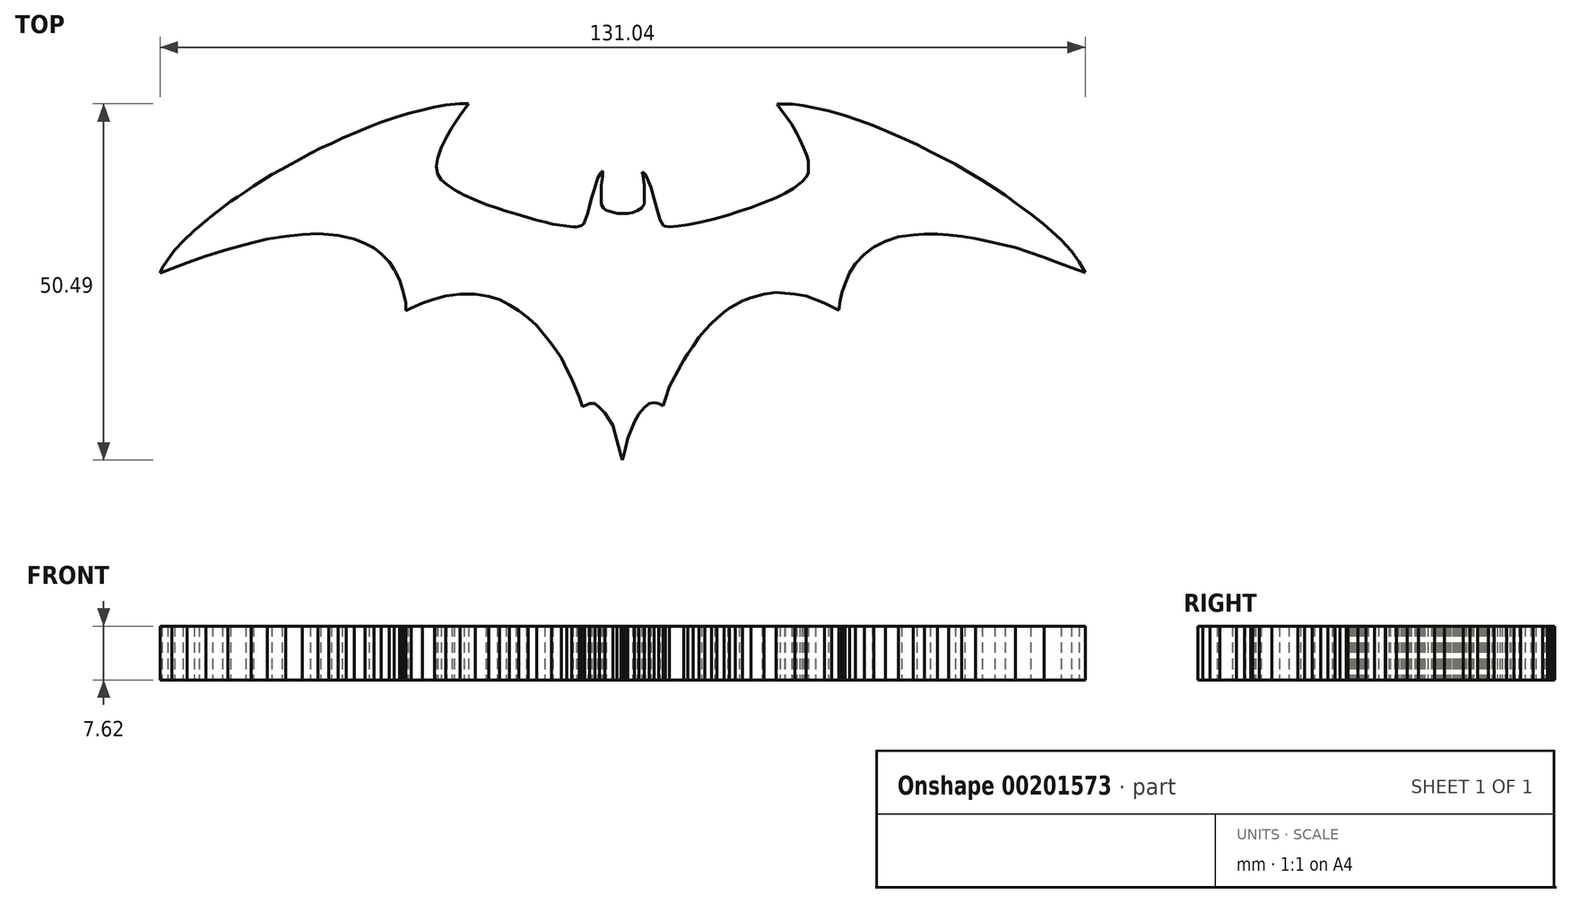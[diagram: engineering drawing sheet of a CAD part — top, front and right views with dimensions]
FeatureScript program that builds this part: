
annotation { "Feature Type Name" : "Feature", "Feature Type Description" : "" }
export const myFeature = defineFeature(function(context is Context, id is Id, definition is map)
    precondition{}
    {
        {
            var Q0;
            Q0=qCreatedBy(makeId("Top.planeOp"),FACE);
            var sketch = newSketch(context, id + "F0", { "sketchPlane" : qUnion([Q0])});
            skLineSegment(sketch, "E0", {"start": v(-30.4, 32.23) * mm, "end": v(-31.57, 30.6) * mm});
            skLineSegment(sketch, "E1", {"start": v(-31.57, 30.6) * mm, "end": v(-32.7, 28.9) * mm});
            skLineSegment(sketch, "E2", {"start": v(-32.7, 28.9) * mm, "end": v(-33.54, 27.45) * mm});
            skLineSegment(sketch, "E3", {"start": v(-33.54, 27.45) * mm, "end": v(-34.23, 26.04) * mm});
            skLineSegment(sketch, "E4", {"start": v(-34.23, 26.04) * mm, "end": v(-34.75, 24.53) * mm});
            skLineSegment(sketch, "E5", {"start": v(-34.75, 24.53) * mm, "end": v(-34.93, 23.39) * mm});
            skLineSegment(sketch, "E6", {"start": v(-34.93, 23.39) * mm, "end": v(-34.75, 22.26) * mm});
            skLineSegment(sketch, "E7", {"start": v(-34.75, 22.26) * mm, "end": v(-34.27, 21.5) * mm});
            skLineSegment(sketch, "E8", {"start": v(-34.27, 21.5) * mm, "end": v(-33.46, 20.8) * mm});
            skLineSegment(sketch, "E9", {"start": v(-33.46, 20.8) * mm, "end": v(-32.4, 20.05) * mm});
            skLineSegment(sketch, "E10", {"start": v(-32.4, 20.05) * mm, "end": v(-30.99, 19.32) * mm});
            skLineSegment(sketch, "E11", {"start": v(-30.99, 19.32) * mm, "end": v(-29.56, 18.68) * mm});
            skLineSegment(sketch, "E12", {"start": v(-29.56, 18.68) * mm, "end": v(-27.88, 18) * mm});
            skLineSegment(sketch, "E13", {"start": v(-27.88, 18) * mm, "end": v(-26.33, 17.45) * mm});
            skLineSegment(sketch, "E14", {"start": v(-26.33, 17.45) * mm, "end": v(-25.01, 17.02) * mm});
            skLineSegment(sketch, "E15", {"start": v(-25.01, 17.02) * mm, "end": v(-23.66, 16.6) * mm});
            skLineSegment(sketch, "E16", {"start": v(-23.66, 16.6) * mm, "end": v(-22.21, 16.2) * mm});
            skLineSegment(sketch, "E17", {"start": v(-22.21, 16.2) * mm, "end": v(-20.75, 15.73) * mm});
            skLineSegment(sketch, "E18", {"start": v(-20.75, 15.73) * mm, "end": v(-19.57, 15.52) * mm});
            skLineSegment(sketch, "E19", {"start": v(-19.57, 15.52) * mm, "end": v(-18.41, 15.18) * mm});
            skLineSegment(sketch, "E20", {"start": v(-18.41, 15.18) * mm, "end": v(-16.98, 14.98) * mm});
            skLineSegment(sketch, "E21", {"start": v(-16.98, 14.98) * mm, "end": v(-15.6, 14.8) * mm});
            skLineSegment(sketch, "E22", {"start": v(-15.6, 14.8) * mm, "end": v(-15.06, 14.8) * mm});
            skLineSegment(sketch, "E23", {"start": v(-15.06, 14.8) * mm, "end": v(-14.4, 14.97) * mm});
            skLineSegment(sketch, "E24", {"start": v(-14.4, 14.97) * mm, "end": v(-14.08, 15.22) * mm});
            skLineSegment(sketch, "E25", {"start": v(-14.08, 15.22) * mm, "end": v(-13.5, 16.75) * mm});
            skLineSegment(sketch, "E26", {"start": v(-13.5, 16.75) * mm, "end": v(-13.23, 17.86) * mm});
            skLineSegment(sketch, "E27", {"start": v(-13.23, 17.86) * mm, "end": v(-12.94, 19.07) * mm});
            skLineSegment(sketch, "E28", {"start": v(-12.94, 19.07) * mm, "end": v(-12.54, 20.18) * mm});
            skLineSegment(sketch, "E29", {"start": v(-12.54, 20.18) * mm, "end": v(-12.07, 21.7) * mm});
            skLineSegment(sketch, "E30", {"start": v(-12.07, 21.7) * mm, "end": v(-11.63, 22.4) * mm});
            skLineSegment(sketch, "E31", {"start": v(-11.63, 22.4) * mm, "end": v(-11.4, 22.7) * mm});
            skLineSegment(sketch, "E32", {"start": v(-11.4, 22.7) * mm, "end": v(-11.4, 21.93) * mm});
            skLineSegment(sketch, "E33", {"start": v(-11.4, 21.93) * mm, "end": v(-11.56, 20.69) * mm});
            skLineSegment(sketch, "E34", {"start": v(-11.56, 20.69) * mm, "end": v(-11.56, 18.7) * mm});
            skLineSegment(sketch, "E35", {"start": v(-11.56, 18.7) * mm, "end": v(-11.56, 17.94) * mm});
            skLineSegment(sketch, "E36", {"start": v(-11.56, 17.94) * mm, "end": v(-11.3, 17.44) * mm});
            skLineSegment(sketch, "E37", {"start": v(-11.3, 17.44) * mm, "end": v(-10.87, 17.18) * mm});
            skLineSegment(sketch, "E38", {"start": v(-10.87, 17.18) * mm, "end": v(-9.98, 16.9) * mm});
            skLineSegment(sketch, "E39", {"start": v(-9.98, 16.9) * mm, "end": v(-9.29, 16.68) * mm});
            skLineSegment(sketch, "E40", {"start": v(-9.29, 16.68) * mm, "end": v(-8.65, 16.68) * mm});
            skLineSegment(sketch, "E41", {"start": v(-8.65, 16.68) * mm, "end": v(-7.86, 16.68) * mm});
            skLineSegment(sketch, "E42", {"start": v(-7.86, 16.68) * mm, "end": v(-7.14, 16.84) * mm});
            skLineSegment(sketch, "E43", {"start": v(-7.14, 16.84) * mm, "end": v(-6.48, 17.1) * mm});
            skLineSegment(sketch, "E44", {"start": v(-6.48, 17.1) * mm, "end": v(-5.84, 17.46) * mm});
            skLineSegment(sketch, "E45", {"start": v(-5.84, 17.46) * mm, "end": v(-5.5, 18.01) * mm});
            skLineSegment(sketch, "E46", {"start": v(-5.5, 18.01) * mm, "end": v(-5.5, 18.92) * mm});
            skLineSegment(sketch, "E47", {"start": v(-5.5, 18.92) * mm, "end": v(-5.5, 19.81) * mm});
            skLineSegment(sketch, "E48", {"start": v(-5.5, 19.81) * mm, "end": v(-5.5, 20.69) * mm});
            skLineSegment(sketch, "E49", {"start": v(-5.5, 20.69) * mm, "end": v(-5.67, 22.08) * mm});
            skLineSegment(sketch, "E50", {"start": v(-5.67, 22.08) * mm, "end": v(-5.8, 22.63) * mm});
            skLineSegment(sketch, "E51", {"start": v(-5.8, 22.63) * mm, "end": v(-5.33, 22.3) * mm});
            skLineSegment(sketch, "E52", {"start": v(-5.33, 22.3) * mm, "end": v(-5.03, 21.6) * mm});
            skLineSegment(sketch, "E53", {"start": v(-5.03, 21.6) * mm, "end": v(-4.5, 20.4) * mm});
            skLineSegment(sketch, "E54", {"start": v(-4.5, 20.4) * mm, "end": v(-4.06, 18.73) * mm});
            skLineSegment(sketch, "E55", {"start": v(-4.06, 18.73) * mm, "end": v(-3.65, 17.16) * mm});
            skLineSegment(sketch, "E56", {"start": v(-3.65, 17.16) * mm, "end": v(-3.28, 15.8) * mm});
            skLineSegment(sketch, "E57", {"start": v(-3.28, 15.8) * mm, "end": v(-2.73, 14.9) * mm});
            skLineSegment(sketch, "E58", {"start": v(-2.73, 14.9) * mm, "end": v(-1.85, 14.78) * mm});
            skLineSegment(sketch, "E59", {"start": v(-1.85, 14.78) * mm, "end": v(-0.63, 14.93) * mm});
            skLineSegment(sketch, "E60", {"start": v(-0.63, 14.93) * mm, "end": v(0.75, 15.1) * mm});
            skLineSegment(sketch, "E61", {"start": v(0.75, 15.1) * mm, "end": v(2.63, 15.52) * mm});
            skLineSegment(sketch, "E62", {"start": v(2.63, 15.52) * mm, "end": v(4.47, 15.97) * mm});
            skLineSegment(sketch, "E63", {"start": v(4.47, 15.97) * mm, "end": v(6.31, 16.46) * mm});
            skLineSegment(sketch, "E64", {"start": v(6.31, 16.46) * mm, "end": v(7.95, 17.02) * mm});
            skLineSegment(sketch, "E65", {"start": v(7.95, 17.02) * mm, "end": v(9.65, 17.56) * mm});
            skLineSegment(sketch, "E66", {"start": v(9.65, 17.56) * mm, "end": v(11.24, 18.16) * mm});
            skLineSegment(sketch, "E67", {"start": v(11.24, 18.16) * mm, "end": v(13.16, 18.95) * mm});
            skLineSegment(sketch, "E68", {"start": v(13.16, 18.95) * mm, "end": v(14.45, 19.6) * mm});
            skLineSegment(sketch, "E69", {"start": v(14.45, 19.6) * mm, "end": v(15.69, 20.29) * mm});
            skLineSegment(sketch, "E70", {"start": v(15.69, 20.29) * mm, "end": v(16.88, 21.23) * mm});
            skLineSegment(sketch, "E71", {"start": v(16.88, 21.23) * mm, "end": v(17.5, 21.93) * mm});
            skLineSegment(sketch, "E72", {"start": v(17.5, 21.93) * mm, "end": v(17.77, 22.5) * mm});
            skLineSegment(sketch, "E73", {"start": v(17.77, 22.5) * mm, "end": v(17.77, 23) * mm});
            skLineSegment(sketch, "E74", {"start": v(17.77, 23) * mm, "end": v(17.77, 23.47) * mm});
            skLineSegment(sketch, "E75", {"start": v(17.77, 23.47) * mm, "end": v(17.77, 24.13) * mm});
            skLineSegment(sketch, "E76", {"start": v(17.77, 24.13) * mm, "end": v(17.57, 24.8) * mm});
            skLineSegment(sketch, "E77", {"start": v(17.57, 24.8) * mm, "end": v(17.15, 25.92) * mm});
            skLineSegment(sketch, "E78", {"start": v(17.15, 25.92) * mm, "end": v(16.55, 27.2) * mm});
            skLineSegment(sketch, "E79", {"start": v(16.55, 27.2) * mm, "end": v(16.09, 28.06) * mm});
            skLineSegment(sketch, "E80", {"start": v(16.09, 28.06) * mm, "end": v(15.38, 29.3) * mm});
            skLineSegment(sketch, "E81", {"start": v(15.38, 29.3) * mm, "end": v(14.4, 30.75) * mm});
            skLineSegment(sketch, "E82", {"start": v(14.4, 30.75) * mm, "end": v(13.76, 31.56) * mm});
            skLineSegment(sketch, "E83", {"start": v(13.76, 31.56) * mm, "end": v(13.34, 32.22) * mm});
            skLineSegment(sketch, "E84", {"start": v(13.34, 32.22) * mm, "end": v(15.52, 32.22) * mm});
            skLineSegment(sketch, "E85", {"start": v(15.52, 32.22) * mm, "end": v(16.91, 32.02) * mm});
            skLineSegment(sketch, "E86", {"start": v(16.91, 32.02) * mm, "end": v(18.77, 31.65) * mm});
            skLineSegment(sketch, "E87", {"start": v(18.77, 31.65) * mm, "end": v(20.59, 31.23) * mm});
            skLineSegment(sketch, "E88", {"start": v(20.59, 31.23) * mm, "end": v(22.8, 30.58) * mm});
            skLineSegment(sketch, "E89", {"start": v(22.8, 30.58) * mm, "end": v(24.85, 29.88) * mm});
            skLineSegment(sketch, "E90", {"start": v(24.85, 29.88) * mm, "end": v(26.81, 29.19) * mm});
            skLineSegment(sketch, "E91", {"start": v(26.81, 29.19) * mm, "end": v(29.05, 28.24) * mm});
            skLineSegment(sketch, "E92", {"start": v(29.05, 28.24) * mm, "end": v(30.97, 27.43) * mm});
            skLineSegment(sketch, "E93", {"start": v(30.97, 27.43) * mm, "end": v(33.1, 26.47) * mm});
            skLineSegment(sketch, "E94", {"start": v(33.1, 26.47) * mm, "end": v(35.01, 25.44) * mm});
            skLineSegment(sketch, "E95", {"start": v(35.01, 25.44) * mm, "end": v(36.8, 24.57) * mm});
            skLineSegment(sketch, "E96", {"start": v(36.8, 24.57) * mm, "end": v(38.6, 23.68) * mm});
            skLineSegment(sketch, "E97", {"start": v(38.6, 23.68) * mm, "end": v(39.93, 22.84) * mm});
            skLineSegment(sketch, "E98", {"start": v(39.93, 22.84) * mm, "end": v(42.38, 21.38) * mm});
            skLineSegment(sketch, "E99", {"start": v(42.38, 21.38) * mm, "end": v(44.2, 20.25) * mm});
            skLineSegment(sketch, "E100", {"start": v(44.2, 20.25) * mm, "end": v(45.63, 19.3) * mm});
            skLineSegment(sketch, "E101", {"start": v(45.63, 19.3) * mm, "end": v(47.5, 17.93) * mm});
            skLineSegment(sketch, "E102", {"start": v(47.5, 17.93) * mm, "end": v(49.23, 16.64) * mm});
            skLineSegment(sketch, "E103", {"start": v(49.23, 16.64) * mm, "end": v(51.06, 15.23) * mm});
            skLineSegment(sketch, "E104", {"start": v(51.06, 15.23) * mm, "end": v(52.26, 14.13) * mm});
            skLineSegment(sketch, "E105", {"start": v(52.26, 14.13) * mm, "end": v(53.55, 12.95) * mm});
            skLineSegment(sketch, "E106", {"start": v(53.55, 12.95) * mm, "end": v(55.05, 11.37) * mm});
            skLineSegment(sketch, "E107", {"start": v(55.05, 11.37) * mm, "end": v(56.1, 9.86) * mm});
            skLineSegment(sketch, "E108", {"start": v(56.1, 9.86) * mm, "end": v(56.97, 8.34) * mm});
            skLineSegment(sketch, "E109", {"start": v(56.97, 8.34) * mm, "end": v(55.04, 9.05) * mm});
            skLineSegment(sketch, "E110", {"start": v(55.04, 9.05) * mm, "end": v(52.82, 9.87) * mm});
            skLineSegment(sketch, "E111", {"start": v(52.82, 9.87) * mm, "end": v(51.15, 10.47) * mm});
            skLineSegment(sketch, "E112", {"start": v(51.15, 10.47) * mm, "end": v(48.93, 11.22) * mm});
            skLineSegment(sketch, "E113", {"start": v(48.93, 11.22) * mm, "end": v(47.1, 11.85) * mm});
            skLineSegment(sketch, "E114", {"start": v(47.1, 11.85) * mm, "end": v(45.24, 12.28) * mm});
            skLineSegment(sketch, "E115", {"start": v(45.24, 12.28) * mm, "end": v(42.95, 12.81) * mm});
            skLineSegment(sketch, "E116", {"start": v(42.95, 12.81) * mm, "end": v(41.42, 13.17) * mm});
            skLineSegment(sketch, "E117", {"start": v(41.42, 13.17) * mm, "end": v(39.45, 13.47) * mm});
            skLineSegment(sketch, "E118", {"start": v(39.45, 13.47) * mm, "end": v(37.64, 13.67) * mm});
            skLineSegment(sketch, "E119", {"start": v(37.64, 13.67) * mm, "end": v(36.02, 13.79) * mm});
            skLineSegment(sketch, "E120", {"start": v(36.02, 13.79) * mm, "end": v(34.22, 13.79) * mm});
            skLineSegment(sketch, "E121", {"start": v(34.22, 13.79) * mm, "end": v(32.62, 13.68) * mm});
            skLineSegment(sketch, "E122", {"start": v(32.62, 13.68) * mm, "end": v(30.51, 13.37) * mm});
            skLineSegment(sketch, "E123", {"start": v(30.51, 13.37) * mm, "end": v(28.66, 12.76) * mm});
            skLineSegment(sketch, "E124", {"start": v(28.66, 12.76) * mm, "end": v(27.06, 11.96) * mm});
            skLineSegment(sketch, "E125", {"start": v(27.06, 11.96) * mm, "end": v(25.68, 10.95) * mm});
            skLineSegment(sketch, "E126", {"start": v(25.68, 10.95) * mm, "end": v(24.4, 9.56) * mm});
            skLineSegment(sketch, "E127", {"start": v(24.4, 9.56) * mm, "end": v(23.63, 8.3) * mm});
            skLineSegment(sketch, "E128", {"start": v(23.63, 8.3) * mm, "end": v(22.94, 6.75) * mm});
            skLineSegment(sketch, "E129", {"start": v(22.94, 6.75) * mm, "end": v(22.51, 5.52) * mm});
            skLineSegment(sketch, "E130", {"start": v(22.51, 5.52) * mm, "end": v(22.29, 4.4) * mm});
            skLineSegment(sketch, "E131", {"start": v(22.29, 4.4) * mm, "end": v(22.1, 3) * mm});
            skLineSegment(sketch, "E132", {"start": v(22.1, 3) * mm, "end": v(21.07, 3.52) * mm});
            skLineSegment(sketch, "E133", {"start": v(21.07, 3.52) * mm, "end": v(20.03, 4.01) * mm});
            skLineSegment(sketch, "E134", {"start": v(20.03, 4.01) * mm, "end": v(18.8, 4.48) * mm});
            skLineSegment(sketch, "E135", {"start": v(18.8, 4.48) * mm, "end": v(17.43, 5) * mm});
            skLineSegment(sketch, "E136", {"start": v(17.43, 5) * mm, "end": v(15.87, 5.26) * mm});
            skLineSegment(sketch, "E137", {"start": v(15.87, 5.26) * mm, "end": v(14.49, 5.39) * mm});
            skLineSegment(sketch, "E138", {"start": v(14.49, 5.39) * mm, "end": v(13.17, 5.5) * mm});
            skLineSegment(sketch, "E139", {"start": v(13.17, 5.5) * mm, "end": v(11.44, 5.26) * mm});
            skLineSegment(sketch, "E140", {"start": v(11.44, 5.26) * mm, "end": v(9.66, 4.8) * mm});
            skLineSegment(sketch, "E141", {"start": v(9.66, 4.8) * mm, "end": v(8.41, 4.33) * mm});
            skLineSegment(sketch, "E142", {"start": v(8.41, 4.33) * mm, "end": v(7.44, 3.77) * mm});
            skLineSegment(sketch, "E143", {"start": v(7.44, 3.77) * mm, "end": v(6.59, 3.3) * mm});
            skLineSegment(sketch, "E144", {"start": v(6.59, 3.3) * mm, "end": v(5.8, 2.74) * mm});
            skLineSegment(sketch, "E145", {"start": v(5.8, 2.74) * mm, "end": v(4.8, 1.85) * mm});
            skLineSegment(sketch, "E146", {"start": v(4.8, 1.85) * mm, "end": v(4.07, 1.16) * mm});
            skLineSegment(sketch, "E147", {"start": v(4.07, 1.16) * mm, "end": v(3.12, 0.15) * mm});
            skLineSegment(sketch, "E148", {"start": v(3.12, 0.15) * mm, "end": v(2.26, -0.85) * mm});
            skLineSegment(sketch, "E149", {"start": v(2.26, -0.85) * mm, "end": v(1.4, -2.07) * mm});
            skLineSegment(sketch, "E150", {"start": v(1.4, -2.07) * mm, "end": v(0.67, -3.16) * mm});
            skLineSegment(sketch, "E151", {"start": v(0.67, -3.16) * mm, "end": v(0.13, -4.1) * mm});
            skLineSegment(sketch, "E152", {"start": v(0.13, -4.1) * mm, "end": v(-0.53, -5.3) * mm});
            skLineSegment(sketch, "E153", {"start": v(-0.53, -5.3) * mm, "end": v(-1.22, -6.55) * mm});
            skLineSegment(sketch, "E154", {"start": v(-1.22, -6.55) * mm, "end": v(-1.91, -7.81) * mm});
            skLineSegment(sketch, "E155", {"start": v(-1.91, -7.81) * mm, "end": v(-2.48, -9.6) * mm});
            skLineSegment(sketch, "E156", {"start": v(-2.48, -9.6) * mm, "end": v(-2.84, -10.55) * mm});
            skLineSegment(sketch, "E157", {"start": v(-2.84, -10.55) * mm, "end": v(-3.42, -10.23) * mm});
            skLineSegment(sketch, "E158", {"start": v(-3.42, -10.23) * mm, "end": v(-4.09, -10.09) * mm});
            skLineSegment(sketch, "E159", {"start": v(-4.09, -10.09) * mm, "end": v(-4.79, -10.23) * mm});
            skLineSegment(sketch, "E160", {"start": v(-4.79, -10.23) * mm, "end": v(-5.47, -10.79) * mm});
            skLineSegment(sketch, "E161", {"start": v(-5.47, -10.79) * mm, "end": v(-6.27, -11.7) * mm});
            skLineSegment(sketch, "E162", {"start": v(-6.27, -11.7) * mm, "end": v(-6.87, -12.8) * mm});
            skLineSegment(sketch, "E163", {"start": v(-6.87, -12.8) * mm, "end": v(-7.38, -14.08) * mm});
            skLineSegment(sketch, "E164", {"start": v(-7.38, -14.08) * mm, "end": v(-7.82, -15.18) * mm});
            skLineSegment(sketch, "E165", {"start": v(-7.82, -15.18) * mm, "end": v(-8.17, -16.57) * mm});
            skLineSegment(sketch, "E166", {"start": v(-8.17, -16.57) * mm, "end": v(-8.4, -17.6) * mm});
            skLineSegment(sketch, "E167", {"start": v(-8.8, -17.6) * mm, "end": v(-9.33, -15.52) * mm});
            skLineSegment(sketch, "E168", {"start": v(-9.33, -15.52) * mm, "end": v(-9.95, -13.36) * mm});
            skLineSegment(sketch, "E169", {"start": v(-9.95, -13.36) * mm, "end": v(-11.05, -11.58) * mm});
            skLineSegment(sketch, "E170", {"start": v(-11.05, -11.58) * mm, "end": v(-11.81, -10.79) * mm});
            skLineSegment(sketch, "E171", {"start": v(-11.81, -10.79) * mm, "end": v(-12.46, -10.23) * mm});
            skLineSegment(sketch, "E172", {"start": v(-12.46, -10.23) * mm, "end": v(-13.26, -10.23) * mm});
            skLineSegment(sketch, "E173", {"start": v(-13.26, -10.23) * mm, "end": v(-13.9, -10.52) * mm});
            skLineSegment(sketch, "E174", {"start": v(-13.9, -10.52) * mm, "end": v(-14.21, -10.66) * mm});
            skLineSegment(sketch, "E175", {"start": v(-14.21, -10.66) * mm, "end": v(-14.66, -9.32) * mm});
            skLineSegment(sketch, "E176", {"start": v(-14.66, -9.32) * mm, "end": v(-15.74, -6.73) * mm});
            skLineSegment(sketch, "E177", {"start": v(-15.74, -6.73) * mm, "end": v(-16.5, -5.4) * mm});
            skLineSegment(sketch, "E178", {"start": v(-16.5, -5.4) * mm, "end": v(-17.25, -3.76) * mm});
            skLineSegment(sketch, "E179", {"start": v(-17.25, -3.76) * mm, "end": v(-18.64, -1.74) * mm});
            skLineSegment(sketch, "E180", {"start": v(-18.64, -1.74) * mm, "end": v(-19.88, -0.22) * mm});
            skLineSegment(sketch, "E181", {"start": v(-19.88, -0.22) * mm, "end": v(-20.71, 0.8) * mm});
            skLineSegment(sketch, "E182", {"start": v(-20.71, 0.8) * mm, "end": v(-21.92, 1.88) * mm});
            skLineSegment(sketch, "E183", {"start": v(-21.92, 1.88) * mm, "end": v(-23.24, 2.91) * mm});
            skLineSegment(sketch, "E184", {"start": v(-23.24, 2.91) * mm, "end": v(-24.6, 3.77) * mm});
            skLineSegment(sketch, "E185", {"start": v(-24.6, 3.77) * mm, "end": v(-26.02, 4.53) * mm});
            skLineSegment(sketch, "E186", {"start": v(-26.02, 4.53) * mm, "end": v(-27.54, 4.94) * mm});
            skLineSegment(sketch, "E187", {"start": v(-27.54, 4.94) * mm, "end": v(-29.42, 5.3) * mm});
            skLineSegment(sketch, "E188", {"start": v(-29.42, 5.3) * mm, "end": v(-31.6, 5.3) * mm});
            skLineSegment(sketch, "E189", {"start": v(-31.6, 5.3) * mm, "end": v(-33.61, 5.04) * mm});
            skLineSegment(sketch, "E190", {"start": v(-33.61, 5.04) * mm, "end": v(-35.2, 4.6) * mm});
            skLineSegment(sketch, "E191", {"start": v(-35.2, 4.6) * mm, "end": v(-36.93, 3.98) * mm});
            skLineSegment(sketch, "E192", {"start": v(-36.93, 3.98) * mm, "end": v(-38.5, 3.28) * mm});
            skLineSegment(sketch, "E193", {"start": v(-38.5, 3.28) * mm, "end": v(-39.27, 2.91) * mm});
            skLineSegment(sketch, "E194", {"start": v(-39.27, 2.91) * mm, "end": v(-39.27, 4.04) * mm});
            skLineSegment(sketch, "E195", {"start": v(-39.27, 4.04) * mm, "end": v(-39.7, 5.87) * mm});
            skLineSegment(sketch, "E196", {"start": v(-39.7, 5.87) * mm, "end": v(-40.16, 7.33) * mm});
            skLineSegment(sketch, "E197", {"start": v(-40.16, 7.33) * mm, "end": v(-40.94, 8.77) * mm});
            skLineSegment(sketch, "E198", {"start": v(-40.94, 8.77) * mm, "end": v(-41.62, 9.85) * mm});
            skLineSegment(sketch, "E199", {"start": v(-41.62, 9.85) * mm, "end": v(-42.77, 10.98) * mm});
            skLineSegment(sketch, "E200", {"start": v(-42.77, 10.98) * mm, "end": v(-43.78, 11.83) * mm});
            skLineSegment(sketch, "E201", {"start": v(-43.78, 11.83) * mm, "end": v(-45.05, 12.48) * mm});
            skLineSegment(sketch, "E202", {"start": v(-45.05, 12.48) * mm, "end": v(-46.55, 13.07) * mm});
            skLineSegment(sketch, "E203", {"start": v(-46.55, 13.07) * mm, "end": v(-47.7, 13.35) * mm});
            skLineSegment(sketch, "E204", {"start": v(-47.7, 13.35) * mm, "end": v(-48.85, 13.57) * mm});
            skLineSegment(sketch, "E205", {"start": v(-48.85, 13.57) * mm, "end": v(-50.17, 13.73) * mm});
            skLineSegment(sketch, "E206", {"start": v(-50.17, 13.73) * mm, "end": v(-51.7, 13.87) * mm});
            skLineSegment(sketch, "E207", {"start": v(-51.7, 13.87) * mm, "end": v(-53.9, 13.72) * mm});
            skLineSegment(sketch, "E208", {"start": v(-53.9, 13.72) * mm, "end": v(-56.29, 13.5) * mm});
            skLineSegment(sketch, "E209", {"start": v(-56.29, 13.5) * mm, "end": v(-58.9, 13.07) * mm});
            skLineSegment(sketch, "E210", {"start": v(-58.9, 13.07) * mm, "end": v(-61.15, 12.54) * mm});
            skLineSegment(sketch, "E211", {"start": v(-61.15, 12.54) * mm, "end": v(-64.47, 11.63) * mm});
            skLineSegment(sketch, "E212", {"start": v(-64.47, 11.63) * mm, "end": v(-67.59, 10.67) * mm});
            skLineSegment(sketch, "E213", {"start": v(-67.59, 10.67) * mm, "end": v(-70.22, 9.74) * mm});
            skLineSegment(sketch, "E214", {"start": v(-70.22, 9.74) * mm, "end": v(-72.38, 8.87) * mm});
            skLineSegment(sketch, "E215", {"start": v(-72.38, 8.87) * mm, "end": v(-74.07, 8.28) * mm});
            skLineSegment(sketch, "E216", {"start": v(-74.07, 8.28) * mm, "end": v(-73.8, 8.96) * mm});
            skLineSegment(sketch, "E217", {"start": v(-73.8, 8.96) * mm, "end": v(-73, 10.16) * mm});
            skLineSegment(sketch, "E218", {"start": v(-73, 10.16) * mm, "end": v(-72.02, 11.52) * mm});
            skLineSegment(sketch, "E219", {"start": v(-72.02, 11.52) * mm, "end": v(-70.8, 12.75) * mm});
            skLineSegment(sketch, "E220", {"start": v(-70.8, 12.75) * mm, "end": v(-69.2, 14.3) * mm});
            skLineSegment(sketch, "E221", {"start": v(-69.2, 14.3) * mm, "end": v(-68.54, 14.86) * mm});
            skLineSegment(sketch, "E222", {"start": v(-68.54, 14.86) * mm, "end": v(-67.75, 15.54) * mm});
            skLineSegment(sketch, "E223", {"start": v(-67.75, 15.54) * mm, "end": v(-66.66, 16.46) * mm});
            skLineSegment(sketch, "E224", {"start": v(-66.66, 16.46) * mm, "end": v(-65.23, 17.5) * mm});
            skLineSegment(sketch, "E225", {"start": v(-65.23, 17.5) * mm, "end": v(-64.1, 18.42) * mm});
            skLineSegment(sketch, "E226", {"start": v(-64.1, 18.42) * mm, "end": v(-63.07, 19.07) * mm});
            skLineSegment(sketch, "E227", {"start": v(-63.07, 19.07) * mm, "end": v(-61.96, 19.79) * mm});
            skLineSegment(sketch, "E228", {"start": v(-61.96, 19.79) * mm, "end": v(-60.83, 20.58) * mm});
            skLineSegment(sketch, "E229", {"start": v(-60.83, 20.58) * mm, "end": v(-59.64, 21.34) * mm});
            skLineSegment(sketch, "E230", {"start": v(-59.64, 21.34) * mm, "end": v(-58.24, 22.24) * mm});
            skLineSegment(sketch, "E231", {"start": v(-58.24, 22.24) * mm, "end": v(-56.8, 22.98) * mm});
            skLineSegment(sketch, "E232", {"start": v(-56.8, 22.98) * mm, "end": v(-54.84, 24.1) * mm});
            skLineSegment(sketch, "E233", {"start": v(-54.84, 24.1) * mm, "end": v(-52.8, 25.24) * mm});
            skLineSegment(sketch, "E234", {"start": v(-52.8, 25.24) * mm, "end": v(-51.33, 25.95) * mm});
            skLineSegment(sketch, "E235", {"start": v(-51.33, 25.95) * mm, "end": v(-49.84, 26.6) * mm});
            skLineSegment(sketch, "E236", {"start": v(-49.84, 26.6) * mm, "end": v(-48.3, 27.38) * mm});
            skLineSegment(sketch, "E237", {"start": v(-48.3, 27.38) * mm, "end": v(-46.15, 28.27) * mm});
            skLineSegment(sketch, "E238", {"start": v(-46.15, 28.27) * mm, "end": v(-44.5, 28.97) * mm});
            skLineSegment(sketch, "E239", {"start": v(-44.5, 28.97) * mm, "end": v(-42.9, 29.58) * mm});
            skLineSegment(sketch, "E240", {"start": v(-42.9, 29.58) * mm, "end": v(-40.81, 30.27) * mm});
            skLineSegment(sketch, "E241", {"start": v(-40.81, 30.27) * mm, "end": v(-38.97, 30.88) * mm});
            skLineSegment(sketch, "E242", {"start": v(-38.97, 30.88) * mm, "end": v(-36.82, 31.4) * mm});
            skLineSegment(sketch, "E243", {"start": v(-36.82, 31.4) * mm, "end": v(-35.32, 31.77) * mm});
            skLineSegment(sketch, "E244", {"start": v(-35.32, 31.77) * mm, "end": v(-33.63, 32.07) * mm});
            skLineSegment(sketch, "E245", {"start": v(-33.63, 32.07) * mm, "end": v(-31.62, 32.24) * mm});
            skLineSegment(sketch, "E246", {"start": v(-31.62, 32.24) * mm, "end": v(-30.4, 32.23) * mm});
            skPoint(sketch, "E247", {"position": v(-8.4, -17.6) * mm});
            skLineSegment(sketch, "E248", {"start": v(-8.8, -17.6) * mm, "end": v(-8.57, -18.25) * mm});
            skLineSegment(sketch, "E249", {"start": v(-8.57, -18.25) * mm, "end": v(-8.4, -17.6) * mm});
            skSolve(sketch);
        }
        {
            var Q0;
            Q0=makeQuery(id+"F0.imprint","IMPRINT",FACE,{"disambiguationData":[TD([[makeQuery(id+"F0.imprint","IMPRINT",EDGE,{"derivedFrom":sQuery(id+"F0.wireOp",EDGE,"E0")}),-1.0]])]});
            extrude(context, id + "F1", {"entities" : qUnion([Q0]), "depth" : 7.62 * mm});
        }
    });
